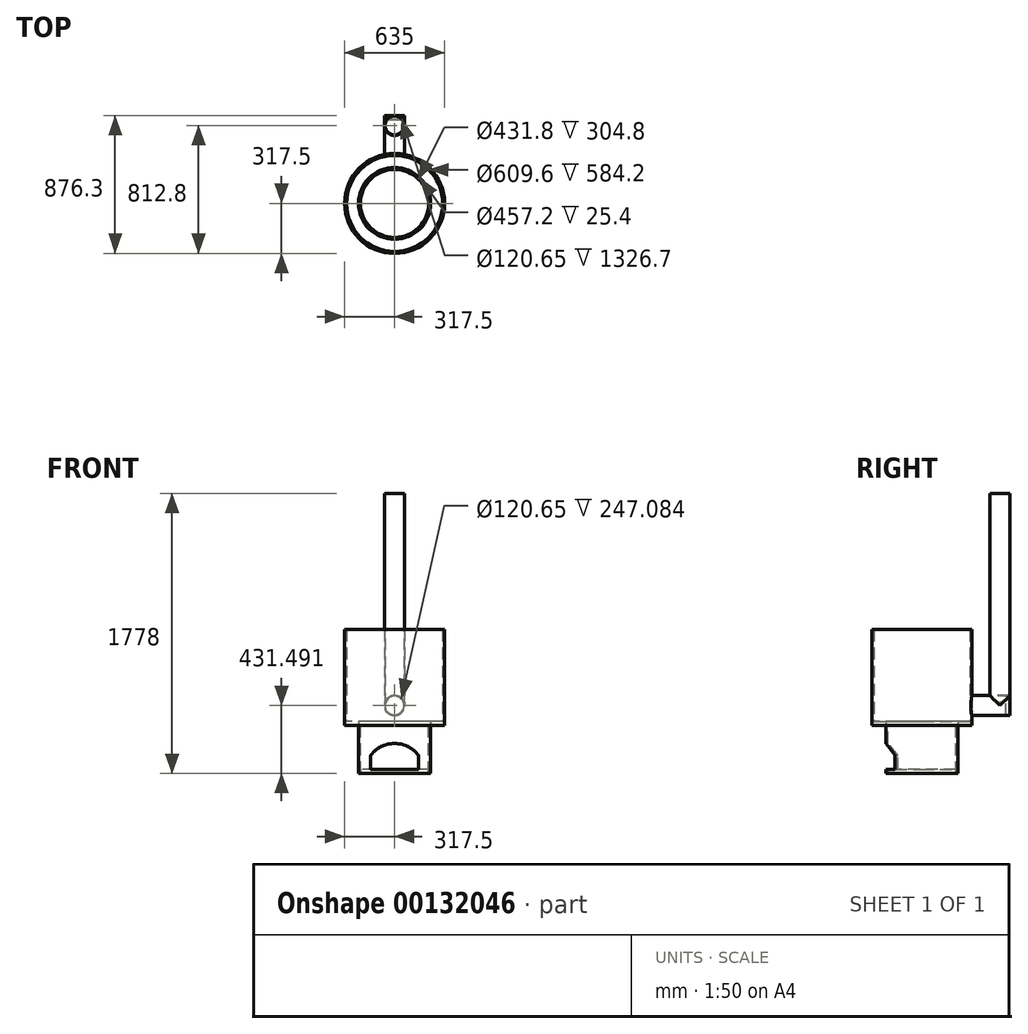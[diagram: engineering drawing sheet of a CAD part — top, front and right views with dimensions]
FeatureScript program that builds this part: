
annotation { "Feature Type Name" : "Feature", "Feature Type Description" : "" }
export const myFeature = defineFeature(function(context is Context, id is Id, definition is map)
    precondition{}
    {
        {
            var Q0;
            Q0=qCreatedBy(makeId("Top.planeOp"),FACE);
            var sketch = newSketch(context, id + "F0", { "sketchPlane" : qUnion([Q0])});
            skCircle(sketch, "E0", {"center": v(0, 0) * mm, "radius": 304.8 * mm});
            skCircle(sketch, "E1", {"center": v(0, 0) * mm, "radius": 317.5 * mm});
            skCircle(sketch, "E2", {"center": v(0, 0) * mm, "radius": 228.6 * mm});
            skCircle(sketch, "E3", {"center": v(0, 0) * mm, "radius": 215.9 * mm});
            skSolve(sketch);
        }
        {
            var Q0;
            Q0=makeQuery(id+"F0.imprint","IMPRINT",FACE,{"disambiguationData":[TD([[makeQuery(id+"F0.imprint","IMPRINT",EDGE,{"derivedFrom":sQuery(id+"F0.wireOp",EDGE,"E0")}),-1.0]])]});
            extrude(context, id + "F1", {"entities" : qUnion([Q0]), "depth" : 609.6 * mm});
        }
        {
            var Q0;
            Q0=makeQuery(id+"F0.imprint","IMPRINT",FACE,{"disambiguationData":[TD([[makeQuery(id+"F0.imprint","IMPRINT",EDGE,{"derivedFrom":sQuery(id+"F0.wireOp",EDGE,"E2")}),1.0]])]});
            extrude(context, id + "F2", {"entities" : qUnion([Q0]), "oppositeDirection" : true, "depth" : 304.8 * mm});
        }
        {
            var Q0;
            Q0=makeQuery(id+"F0.imprint","IMPRINT",FACE,{"disambiguationData":[TD([[makeQuery(id+"F0.imprint","IMPRINT",EDGE,{"derivedFrom":sQuery(id+"F0.wireOp",EDGE,"E0")}),1.0]])]});
            extrude(context, id + "F3", {"entities" : qUnion([Q0]), "operationType" : NewBodyOperationType.ADD, "depth" : 25.4 * mm});
        }
        {
            var Q0;
            Q0=makeQuery(id+"F2.opExtrude","CAP_FACE",FACE,{"disambiguationData":[OSD([sQuery(id+"F0.wireOp",EDGE,"E2"),sQuery(id+"F0.wireOp",EDGE,"E3")])],"isStart":false});
            var sketch = newSketch(context, id + "F4", { "sketchPlane" : qUnion([Q0])});
            skCircle(sketch, "E4", {"center": v(0, 0) * mm, "radius": 228.51 * mm});
            skSolve(sketch);
        }
        {
            var Q0;
            Q0=makeQuery(id+"F4.imprint","IMPRINT",FACE,{"disambiguationData":[TD([[makeQuery(id+"F4.imprint","IMPRINT",EDGE,{"derivedFrom":makeQuery(id+"F2.opExtrude","CAP_EDGE",EDGE,{"disambiguationData":[OSD([sQuery(id+"F0.wireOp",EDGE,"E3")])],"isStart":false})}),-1.0]])]});
            extrude(context, id + "F5", {"entities" : qUnion([Q0]), "oppositeDirection" : true, "depth" : 25.4 * mm});
        }
        {
            var Q0;
            Q0=qCreatedBy(makeId("Front.planeOp"),FACE);
            cPlane(context, id + "F6", {"entities" : qUnion([Q0]), "cplaneType" : CPlaneType.OFFSET, "offset" : 355.6 * mm, "oppositeDirection" : true, "width" : 152.4 * mm, "height" : 152.4 * mm});
        }
        {
            var Q0;
            Q0=qCreatedBy(id+"F6.planeOp",FACE);
            var sketch = newSketch(context, id + "F7", { "sketchPlane" : qUnion([Q0])});
            skLineSegment(sketch, "E5.0", {"start": v(-228.6, -304.8) * mm, "end": v(228.6, -304.8) * mm});
            skLineSegment(sketch, "E5.1", {"start": v(-215.9, -304.8) * mm, "end": v(215.9, -304.8) * mm});
            skArc(sketch, "E6", {"start": v(149.84, -187.17) * mm, "mid": v(0, -114.3) * mm, "end": v(-149.84, -187.17) * mm});
            skLineSegment(sketch, "E7.left", {"start": v(149.84, -187.17) * mm, "end": v(149.84, -304.8) * mm});
            skLineSegment(sketch, "E7.right", {"start": v(-149.84, -187.17) * mm, "end": v(-149.84, -304.8) * mm});
            skPoint(sketch, "E8.orphan", {"position": v(-149.84, -422.43) * mm});
            skPoint(sketch, "E9.orphan", {"position": v(149.84, -422.43) * mm});
            skSolve(sketch);
        }
        {
            var Q0;
            Q0=makeQuery(id+"F7.imprint","IMPRINT",FACE,{"disambiguationData":[TD([[makeQuery(id+"F7.imprint","IMPRINT",EDGE,{"derivedFrom":sQuery(id+"F7.wireOp",EDGE,"E6")}),1.0]])]});
            extrude(context, id + "F8", {"entities" : qUnion([Q0]), "operationType" : NewBodyOperationType.REMOVE, "oppositeDirection" : true, "depth" : 254 * mm});
        }
        {
            var Q0;
            Q0=qCreatedBy(id+"F6.planeOp",FACE);
            var sketch = newSketch(context, id + "F9", { "sketchPlane" : qUnion([Q0])});
            skLineSegment(sketch, "E10.0", {"start": v(-317.5, 0) * mm, "end": v(317.5, 0) * mm});
            skCircle(sketch, "E11", {"center": v(0, 126.7) * mm, "radius": 60.33 * mm});
            skCircle(sketch, "E12", {"center": v(0, 126.7) * mm, "radius": 63.5 * mm});
            skSolve(sketch);
        }
        {
            var Q0;
            Q0=makeQuery(id+"F9.imprint","IMPRINT",FACE,{"disambiguationData":[TD([[makeQuery(id+"F9.imprint","IMPRINT",EDGE,{"derivedFrom":sQuery(id+"F9.wireOp",EDGE,"E11")}),-1.0]])]});
            var Q1;
            Q1=makeQuery(id+"F1.opExtrude","SWEPT_FACE",FACE,{"disambiguationData":[OSD([sQuery(id+"F0.wireOp",EDGE,"E1")])]});
            extrude(context, id + "F10", {"entities" : qUnion([Q0]), "operationType" : NewBodyOperationType.ADD, "oppositeDirection" : true, "depth" : 203.2 * mm, "hasSecondDirection" : true, "secondDirectionBound" : SecondDirectionBoundingType.UP_TO_SURFACE, "secondDirectionOppositeDirection" : false, "secondDirectionBoundEntityFace" : qUnion([Q1]), "secondDirectionDepth" : 25.4 * mm});
        }
        {
            var Q0;
            Q0=qCreatedBy(makeId("Top.planeOp"),FACE);
            cPlane(context, id + "F11", {"entities" : qUnion([Q0]), "cplaneType" : CPlaneType.OFFSET, "offset" : 203.2 * mm, "width" : 152.4 * mm, "height" : 152.4 * mm});
        }
        {
            var Q0;
            Q0=qCreatedBy(id+"F11.planeOp",FACE);
            var sketch = newSketch(context, id + "F12", { "sketchPlane" : qUnion([Q0])});
            skLineSegment(sketch, "E13.0", {"start": v(63.5, 558.8) * mm, "end": v(-63.5, 558.8) * mm});
            skCircle(sketch, "E14", {"center": v(0, 495.3) * mm, "radius": 63.5 * mm});
            skPoint(sketch, "E14.centerSnap0", {"position": v(0, 558.8) * mm});
            skCircle(sketch, "E15", {"center": v(0, 495.3) * mm, "radius": 60.33 * mm});
            skSolve(sketch);
        }
        {
            var Q0;
            Q0=makeQuery(id+"F12.imprint","IMPRINT",FACE,{"disambiguationData":[TD([[makeQuery(id+"F12.imprint","IMPRINT",EDGE,{"derivedFrom":sQuery(id+"F12.wireOp",EDGE,"E14")}),1.0]])]});
            var Q1;
            Q1=makeQuery(id+"F10.opExtrude","SWEPT_FACE",FACE,{"disambiguationData":[OSD([sQuery(id+"F9.wireOp",EDGE,"E12")])]});
            extrude(context, id + "F13", {"entities" : qUnion([Q0]), "operationType" : NewBodyOperationType.ADD, "depth" : 1270 * mm, "hasSecondDirection" : true, "secondDirectionBound" : SecondDirectionBoundingType.UP_TO_SURFACE, "secondDirectionOppositeDirection" : true, "secondDirectionBoundEntityFace" : qUnion([Q1]), "secondDirectionDepth" : 25.4 * mm});
        }
        {
            var Q0;
            Q0=makeQuery(id+"F10.opExtrude","CAP_FACE",FACE,{"disambiguationData":[OSD([sQuery(id+"F9.wireOp",EDGE,"E11"),sQuery(id+"F9.wireOp",EDGE,"E12")])],"isStart":false});
            var sketch = newSketch(context, id + "F14", { "sketchPlane" : qUnion([Q0])});
            skCircle(sketch, "E16.0", {"center": v(0, 126.7) * mm, "radius": 63.5 * mm});
            skSolve(sketch);
        }
        {
            var Q0;
            Q0=makeQuery(id+"F14.imprint","IMPRINT",FACE,{"disambiguationData":[TD([[makeQuery(id+"F14.imprint","IMPRINT",EDGE,{"derivedFrom":makeQuery(id+"F10.opExtrude","CAP_EDGE",EDGE,{"disambiguationData":[OSD([sQuery(id+"F9.wireOp",EDGE,"E11")])],"isStart":false})}),-1.0]])]});
            extrude(context, id + "F15", {"entities" : qUnion([Q0]), "oppositeDirection" : true, "depth" : 25.4 * mm});
        }
        {
            var Q0;
            Q0=qCreatedBy(makeId("Front.planeOp"),FACE);
            var sketch = newSketch(context, id + "F16", { "sketchPlane" : qUnion([Q0])});
            skLineSegment(sketch, "E17.0", {"start": v(-228.6, -304.8) * mm, "end": v(-152.4, -304.8) * mm});
            skArc(sketch, "E18", {"start": v(152.4, -190.5) * mm, "mid": v(0, -114.3) * mm, "end": v(-152.4, -190.5) * mm});
            skLineSegment(sketch, "E19.left", {"start": v(152.4, -190.5) * mm, "end": v(152.4, -279.4) * mm});
            skLineSegment(sketch, "E19.right", {"start": v(-152.4, -190.5) * mm, "end": v(-152.4, -279.4) * mm});
            skPoint(sketch, "E20.orphan", {"position": v(-152.4, -419.1) * mm});
            skPoint(sketch, "E21.orphan", {"position": v(152.4, -419.1) * mm});
            skLineSegment(sketch, "E22.bottom", {"start": v(-152.4, -279.4) * mm, "end": v(152.4, -279.4) * mm});
            skLineSegment(sketch, "E22.left", {"start": v(-152.4, -279.4) * mm, "end": v(-152.4, -190.5) * mm});
            skLineSegment(sketch, "E22.right", {"start": v(152.4, -279.4) * mm, "end": v(152.4, -190.5) * mm});
            skPoint(sketch, "E23.orphan", {"position": v(-152.4, -304.8) * mm});
            skLineSegment(sketch, "E24.trimOffspring", {"start": v(152.4, -304.8) * mm, "end": v(228.6, -304.8) * mm});
            skSolve(sketch);
        }
        {
            var Q0;
            Q0 = qSketchRegion(id + "F16", true);
            extrude(context, id + "F17", {"entities" : qUnion([Q0]), "operationType" : NewBodyOperationType.REMOVE, "depth" : 508 * mm});
        }
    });
